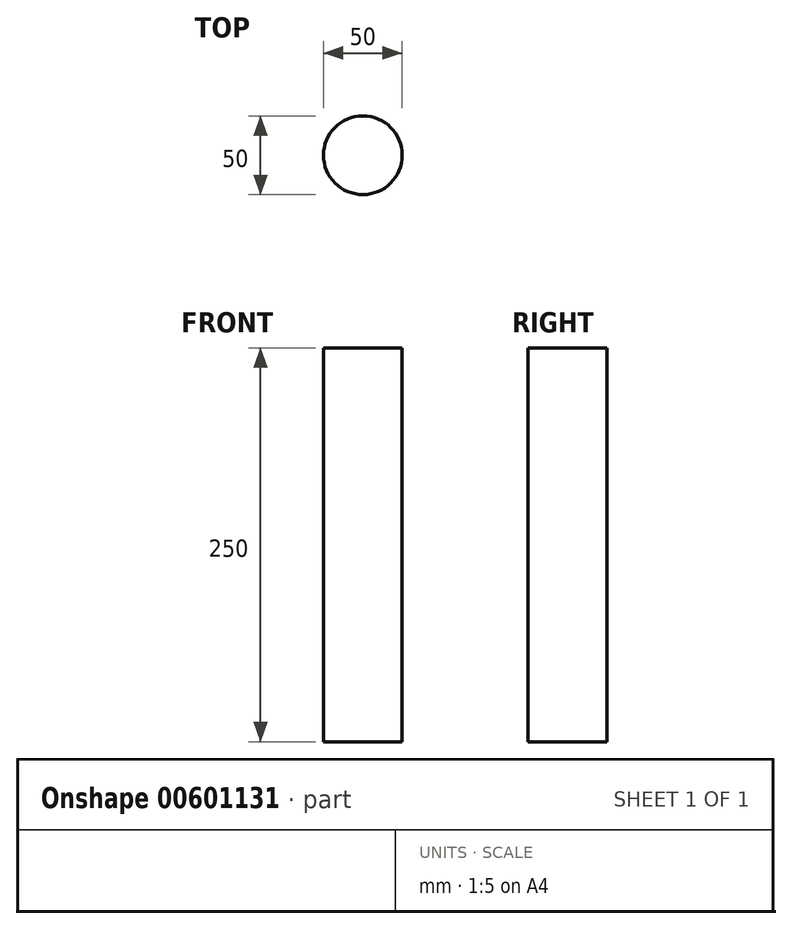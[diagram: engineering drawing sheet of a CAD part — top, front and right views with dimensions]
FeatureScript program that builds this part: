
annotation { "Feature Type Name" : "Feature", "Feature Type Description" : "" }
export const myFeature = defineFeature(function(context is Context, id is Id, definition is map)
    precondition{}
    {
        {
            var Q0;
            Q0=qCreatedBy(makeId("Top.planeOp"),FACE);
            var sketch = newSketch(context, id + "F0", { "sketchPlane" : qUnion([Q0])});
            skCircle(sketch, "E0", {"center": v(0, 0) * mm, "radius": 25 * mm});
            skSolve(sketch);
        }
        {
            var Q0;
            Q0=makeQuery(id+"F0.imprint","IMPRINT",FACE,{"disambiguationData":[TD([[makeQuery(id+"F0.imprint","IMPRINT",EDGE,{"derivedFrom":sQuery(id+"F0.wireOp",EDGE,"E0")}),1.0]])]});
            extrude(context, id + "F1", {"entities" : qUnion([Q0]), "depth" : 250 * mm, "offsetDistance" : 25 * mm});
        }
    });
